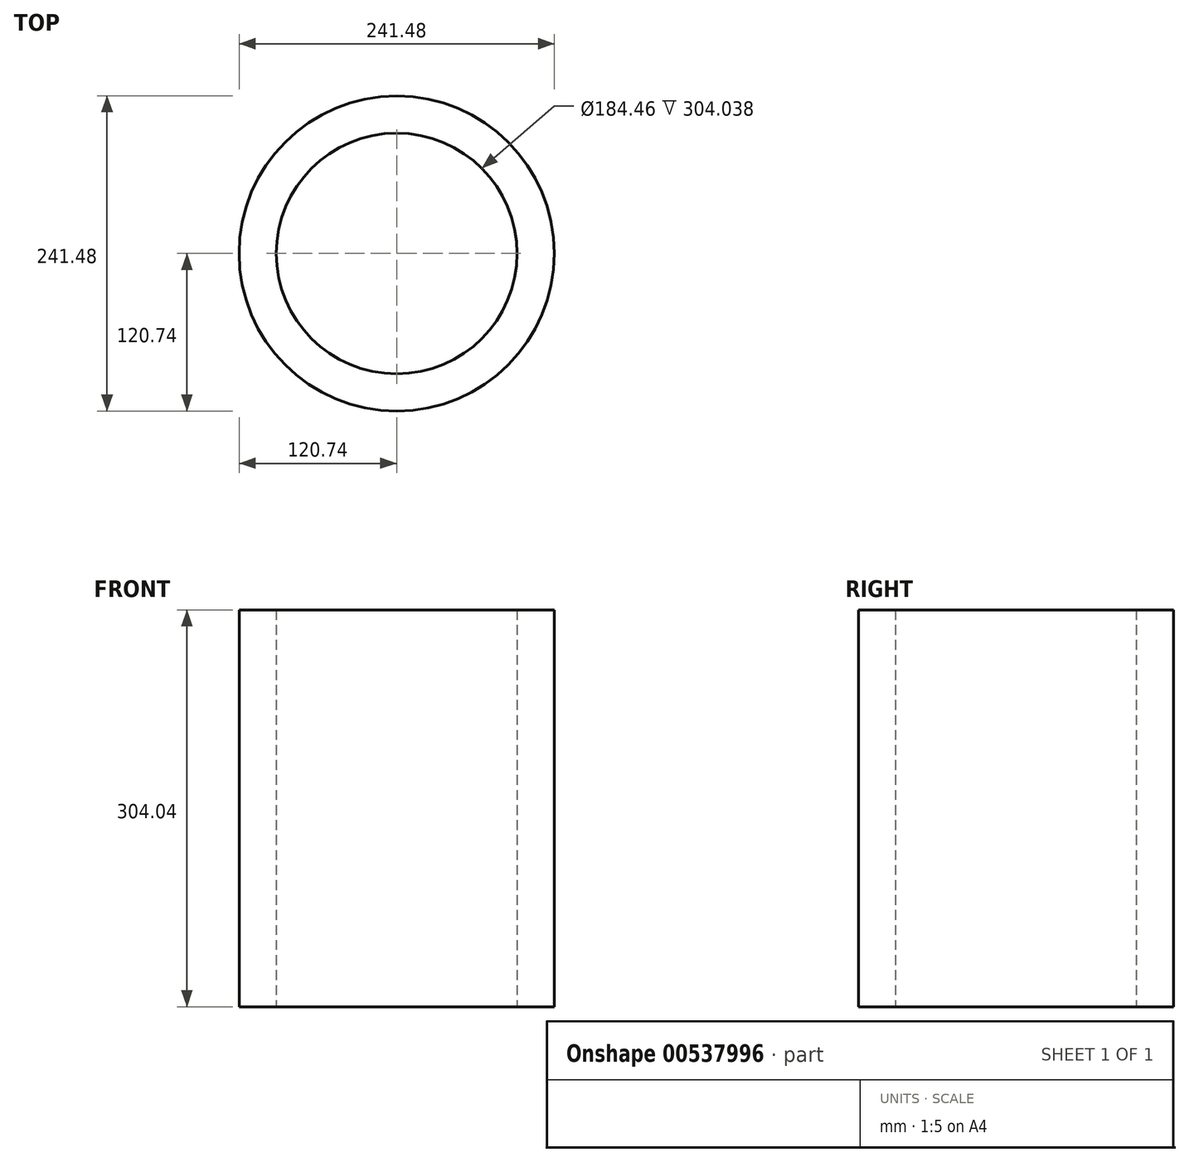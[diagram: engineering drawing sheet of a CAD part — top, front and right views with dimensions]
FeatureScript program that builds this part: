
annotation { "Feature Type Name" : "Feature", "Feature Type Description" : "" }
export const myFeature = defineFeature(function(context is Context, id is Id, definition is map)
    precondition{}
    {
        {
            var Q0;
            Q0=qCreatedBy(makeId("Top.planeOp"),FACE);
            var sketch = newSketch(context, id + "F0", { "sketchPlane" : qUnion([Q0])});
            skCircle(sketch, "E0", {"center": v(0, 0) * mm, "radius": 120.74 * mm});
            skCircle(sketch, "E1", {"center": v(0, 0) * mm, "radius": 92.23 * mm});
            skSolve(sketch);
        }
        {
            var Q0;
            Q0=makeQuery(id+"F0.imprint","IMPRINT",FACE,{"disambiguationData":[TD([[makeQuery(id+"F0.imprint","IMPRINT",EDGE,{"derivedFrom":sQuery(id+"F0.wireOp",EDGE,"E0")}),1.0]])]});
            extrude(context, id + "F1", {"entities" : qUnion([Q0]), "depth" : 304.04 * mm, "offsetDistance" : 25.4 * mm});
        }
    });
